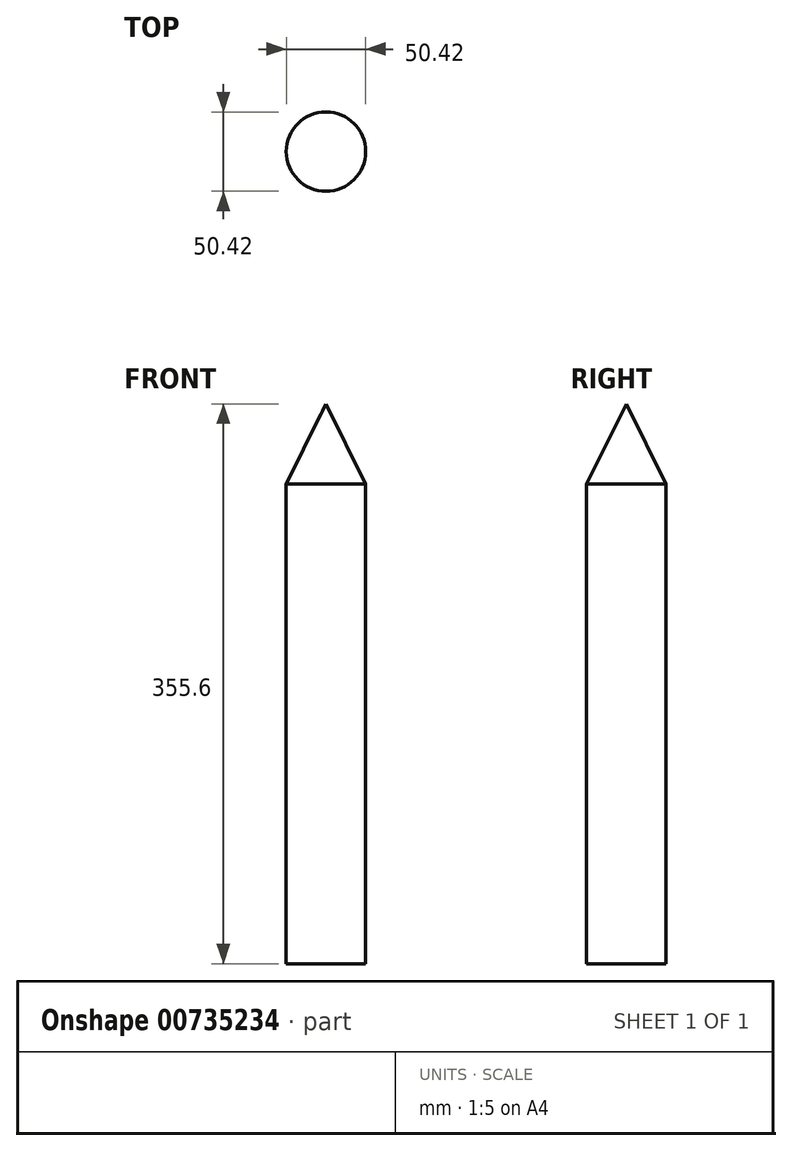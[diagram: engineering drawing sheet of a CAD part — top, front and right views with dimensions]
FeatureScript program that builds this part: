
annotation { "Feature Type Name" : "Feature", "Feature Type Description" : "" }
export const myFeature = defineFeature(function(context is Context, id is Id, definition is map)
    precondition{}
    {
        {
            var Q0;
            Q0=qCreatedBy(makeId("Top.planeOp"),FACE);
            var sketch = newSketch(context, id + "F0", { "sketchPlane" : qUnion([Q0])});
            skCircle(sketch, "E0", {"center": v(0, 0) * mm, "radius": 25.4 * mm});
            skSolve(sketch);
        }
        {
            var Q0;
            Q0=qCreatedBy(makeId("Front.planeOp"),FACE);
            var sketch = newSketch(context, id + "F1", { "sketchPlane" : qUnion([Q0])});
            skLineSegment(sketch, "E1", {"start": v(0, 0) * mm, "end": v(0, 50.8) * mm});
            skLineSegment(sketch, "E2", {"start": v(0, 0) * mm, "end": v(-25.21, 0) * mm});
            skLineSegment(sketch, "E3", {"start": v(0, 50.8) * mm, "end": v(-25.21, 0) * mm});
            skSolve(sketch);
        }
        {
            var Q0;
            Q0=makeQuery(id+"F1.imprint","IMPRINT",FACE,{"disambiguationData":[TD([[makeQuery(id+"F1.imprint","IMPRINT",EDGE,{"derivedFrom":sQuery(id+"F1.wireOp",EDGE,"E1")}),1.0]])]});
            var Q1;
            Q1=sQuery(id+"F0.wireOp",EDGE,"E0");
            revolve(context, id + "F2", {"surfaceOperationType" : NewSurfaceOperationType.NEW, "entities" : qUnion([Q0]), "axis" : qUnion([Q1]), "revolveType" : RevolveType.FULL});
        }
        {
            var Q0;
            Q0=makeQuery(id+"F2.opRevolve","SWEPT_FACE",FACE,{"disambiguationData":[OSD([sQuery(id+"F1.wireOp",EDGE,"E2")])]});
            extrude(context, id + "F3", {"entities" : qUnion([Q0]), "operationType" : NewBodyOperationType.ADD, "depth" : 304.8 * mm, "offsetDistance" : 25.4 * mm});
        }
    });
